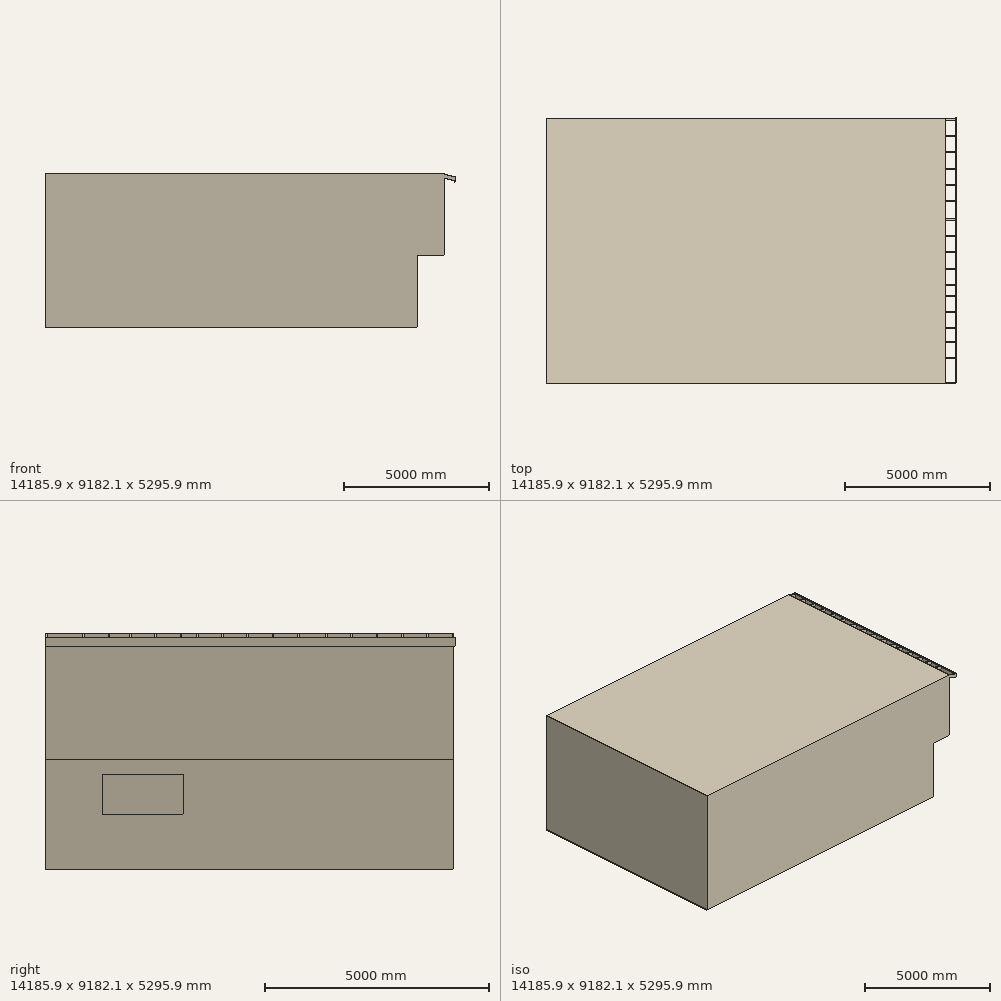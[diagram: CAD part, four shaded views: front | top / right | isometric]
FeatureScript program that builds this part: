
annotation { "Feature Type Name" : "Feature", "Feature Type Description" : "" }
export const myFeature = defineFeature(function(context is Context, id is Id, definition is map)
    precondition{}
    {
        {
            var Q0;
            Q0=qCreatedBy(makeId("Top.planeOp"),FACE);
            var sketch = newSketch(context, id + "F0", { "sketchPlane" : qUnion([Q0])});
            skLineSegment(sketch, "E0.bottom", {"start": v(6438.9, -4572) * mm, "end": v(-6438.9, -4572) * mm});
            skLineSegment(sketch, "E0.top", {"start": v(6438.9, 4572) * mm, "end": v(-6438.9, 4572) * mm});
            skLineSegment(sketch, "E0.left", {"start": v(6438.9, -4572) * mm, "end": v(6438.9, 4572) * mm});
            skLineSegment(sketch, "E0.right", {"start": v(-6438.9, -4572) * mm, "end": v(-6438.9, 4572) * mm});
            skPoint(sketch, "E0.middle", {"position": v(0, 0) * mm});
            skSolve(sketch);
        }
        {
            var Q0;
            Q0=makeQuery(id+"F0.imprint","IMPRINT",FACE,{"disambiguationData":[TD([[makeQuery(id+"F0.imprint","IMPRINT",EDGE,{"derivedFrom":sQuery(id+"F0.wireOp",EDGE,"E0.bottom")}),-1.0]])]});
            extrude(context, id + "F1", {"entities" : qUnion([Q0]), "depth" : 5295.9 * mm});
        }
        {
            var Q0;
            Q0=makeQuery(id+"F1.opExtrude","SWEPT_FACE",FACE,{"disambiguationData":[OSD([sQuery(id+"F0.wireOp",EDGE,"E0.left")])]});
            var sketch = newSketch(context, id + "F2", { "sketchPlane" : qUnion([Q0])});
            skLineSegment(sketch, "E1.bottom", {"start": v(-4572, 2476.5) * mm, "end": v(4572, 2476.5) * mm});
            skLineSegment(sketch, "E1.top", {"start": v(-4572, 5295.9) * mm, "end": v(4572, 5295.9) * mm});
            skLineSegment(sketch, "E1.left", {"start": v(-4572, 2476.5) * mm, "end": v(-4572, 5295.9) * mm});
            skLineSegment(sketch, "E1.right", {"start": v(4572, 2476.5) * mm, "end": v(4572, 5295.9) * mm});
            skSolve(sketch);
        }
        {
            var Q0;
            Q0 = qSketchRegion(id + "F2", true);
            extrude(context, id + "F3", {"entities" : qUnion([Q0]), "operationType" : NewBodyOperationType.ADD, "depth" : 914.4 * mm});
        }
        {
            var Q0;
            Q0=makeQuery(id+"F1.opExtrude","SWEPT_FACE",FACE,{"disambiguationData":[OSD([sQuery(id+"F0.wireOp",EDGE,"E0.left")])]});
            var sketch = newSketch(context, id + "F4", { "sketchPlane" : qUnion([Q0])});
            skLineSegment(sketch, "E2.bottom", {"start": v(-3289.3, 1244.6) * mm, "end": v(-1485.9, 1244.6) * mm});
            skLineSegment(sketch, "E2.top", {"start": v(-3289.3, 2133.6) * mm, "end": v(-1485.9, 2133.6) * mm});
            skLineSegment(sketch, "E2.left", {"start": v(-3289.3, 1244.6) * mm, "end": v(-3289.3, 2133.6) * mm});
            skLineSegment(sketch, "E2.right", {"start": v(-1485.9, 1244.6) * mm, "end": v(-1485.9, 2133.6) * mm});
            skSolve(sketch);
        }
        {
            var Q0;
            Q0 = qSketchRegion(id + "F4", true);
            extrude(context, id + "F5", {"entities" : qUnion([Q0]), "operationType" : NewBodyOperationType.REMOVE, "oppositeDirection" : true, "depth" : 30.48 * mm});
        }
        {
            var Q0;
            Q0=makeQuery(id+"F3.opExtrude","CAP_FACE",FACE,{"disambiguationData":[OSD([sQuery(id+"F2.wireOp",EDGE,"E1.bottom"),sQuery(id+"F2.wireOp",EDGE,"E1.top"),sQuery(id+"F2.wireOp",EDGE,"E1.left"),sQuery(id+"F2.wireOp",EDGE,"E1.right")])],"isStart":false});
            var sketch = newSketch(context, id + "F6", { "sketchPlane" : qUnion([Q0])});
            skLineSegment(sketch, "E3.bottom", {"start": v(-4572, 5295.9) * mm, "end": v(-4533.9, 5295.9) * mm});
            skLineSegment(sketch, "E3.top", {"start": v(-4572, 5156.2) * mm, "end": v(-4533.9, 5156.2) * mm});
            skLineSegment(sketch, "E3.left", {"start": v(-4572, 5295.9) * mm, "end": v(-4572, 5156.2) * mm});
            skLineSegment(sketch, "E3.right", {"start": v(-4533.9, 5295.9) * mm, "end": v(-4533.9, 5156.2) * mm});
            skLineSegment(sketch, "E4.bottom", {"start": v(-3733.8, 5295.9) * mm, "end": v(-3695.7, 5295.9) * mm});
            skLineSegment(sketch, "E4.top", {"start": v(-3733.8, 5156.2) * mm, "end": v(-3695.7, 5156.2) * mm});
            skLineSegment(sketch, "E4.left", {"start": v(-3733.8, 5295.9) * mm, "end": v(-3733.8, 5156.2) * mm});
            skLineSegment(sketch, "E4.right", {"start": v(-3695.7, 5295.9) * mm, "end": v(-3695.7, 5156.2) * mm});
            skLineSegment(sketch, "E5.bottom", {"start": v(-3167.38, 5156.2) * mm, "end": v(-3129.28, 5156.2) * mm});
            skLineSegment(sketch, "E5.top", {"start": v(-3167.38, 5295.9) * mm, "end": v(-3129.28, 5295.9) * mm});
            skLineSegment(sketch, "E5.left", {"start": v(-3167.38, 5156.2) * mm, "end": v(-3167.38, 5295.9) * mm});
            skLineSegment(sketch, "E5.right", {"start": v(-3129.28, 5156.2) * mm, "end": v(-3129.28, 5295.9) * mm});
            skLineSegment(sketch, "E6.bottom", {"start": v(-2692.4, 5156.2) * mm, "end": v(-2654.3, 5156.2) * mm});
            skLineSegment(sketch, "E6.top", {"start": v(-2692.4, 5295.9) * mm, "end": v(-2654.3, 5295.9) * mm});
            skLineSegment(sketch, "E6.left", {"start": v(-2692.4, 5156.2) * mm, "end": v(-2692.4, 5295.9) * mm});
            skLineSegment(sketch, "E6.right", {"start": v(-2654.3, 5156.2) * mm, "end": v(-2654.3, 5295.9) * mm});
            skLineSegment(sketch, "E7.bottom", {"start": v(-2125.98, 5156.2) * mm, "end": v(-2087.88, 5156.2) * mm});
            skLineSegment(sketch, "E7.top", {"start": v(-2125.98, 5295.9) * mm, "end": v(-2087.88, 5295.9) * mm});
            skLineSegment(sketch, "E7.left", {"start": v(-2125.98, 5156.2) * mm, "end": v(-2125.98, 5295.9) * mm});
            skLineSegment(sketch, "E7.right", {"start": v(-2087.88, 5156.2) * mm, "end": v(-2087.88, 5295.9) * mm});
            skLineSegment(sketch, "E8.bottom", {"start": v(-1559.56, 5156.2) * mm, "end": v(-1521.46, 5156.2) * mm});
            skLineSegment(sketch, "E8.top", {"start": v(-1559.56, 5295.9) * mm, "end": v(-1521.46, 5295.9) * mm});
            skLineSegment(sketch, "E8.left", {"start": v(-1559.56, 5156.2) * mm, "end": v(-1559.56, 5295.9) * mm});
            skLineSegment(sketch, "E8.right", {"start": v(-1521.46, 5156.2) * mm, "end": v(-1521.46, 5295.9) * mm});
            skLineSegment(sketch, "E9.bottom", {"start": v(-1193.8, 5156.2) * mm, "end": v(-1155.7, 5156.2) * mm});
            skLineSegment(sketch, "E9.top", {"start": v(-1193.8, 5295.9) * mm, "end": v(-1155.7, 5295.9) * mm});
            skLineSegment(sketch, "E9.left", {"start": v(-1193.8, 5156.2) * mm, "end": v(-1193.8, 5295.9) * mm});
            skLineSegment(sketch, "E9.right", {"start": v(-1155.7, 5156.2) * mm, "end": v(-1155.7, 5295.9) * mm});
            skLineSegment(sketch, "E10.bottom", {"start": v(-627.38, 5156.2) * mm, "end": v(-589.28, 5156.2) * mm});
            skLineSegment(sketch, "E10.top", {"start": v(-627.38, 5295.9) * mm, "end": v(-589.28, 5295.9) * mm});
            skLineSegment(sketch, "E10.left", {"start": v(-627.38, 5156.2) * mm, "end": v(-627.38, 5295.9) * mm});
            skLineSegment(sketch, "E10.right", {"start": v(-589.28, 5156.2) * mm, "end": v(-589.28, 5295.9) * mm});
            skLineSegment(sketch, "E11.bottom", {"start": v(-60.96, 5156.2) * mm, "end": v(-22.86, 5156.2) * mm});
            skLineSegment(sketch, "E11.top", {"start": v(-60.96, 5295.9) * mm, "end": v(-22.86, 5295.9) * mm});
            skLineSegment(sketch, "E11.left", {"start": v(-60.96, 5156.2) * mm, "end": v(-60.96, 5295.9) * mm});
            skLineSegment(sketch, "E11.right", {"start": v(-22.86, 5156.2) * mm, "end": v(-22.86, 5295.9) * mm});
            skLineSegment(sketch, "E12.bottom", {"start": v(505.46, 5156.2) * mm, "end": v(543.56, 5156.2) * mm});
            skLineSegment(sketch, "E12.top", {"start": v(505.46, 5295.9) * mm, "end": v(543.56, 5295.9) * mm});
            skLineSegment(sketch, "E12.left", {"start": v(505.46, 5156.2) * mm, "end": v(505.46, 5295.9) * mm});
            skLineSegment(sketch, "E12.right", {"start": v(543.56, 5156.2) * mm, "end": v(543.56, 5295.9) * mm});
            skLineSegment(sketch, "E13.bottom", {"start": v(1071.88, 5156.2) * mm, "end": v(1109.98, 5156.2) * mm});
            skLineSegment(sketch, "E13.top", {"start": v(1071.88, 5295.9) * mm, "end": v(1109.98, 5295.9) * mm});
            skLineSegment(sketch, "E13.left", {"start": v(1071.88, 5156.2) * mm, "end": v(1071.88, 5295.9) * mm});
            skLineSegment(sketch, "E13.right", {"start": v(1109.98, 5156.2) * mm, "end": v(1109.98, 5295.9) * mm});
            skLineSegment(sketch, "E14.bottom", {"start": v(1701.8, 5156.2) * mm, "end": v(1739.9, 5156.2) * mm});
            skLineSegment(sketch, "E14.top", {"start": v(1701.8, 5295.9) * mm, "end": v(1739.9, 5295.9) * mm});
            skLineSegment(sketch, "E14.left", {"start": v(1701.8, 5156.2) * mm, "end": v(1701.8, 5295.9) * mm});
            skLineSegment(sketch, "E14.right", {"start": v(1739.9, 5156.2) * mm, "end": v(1739.9, 5295.9) * mm});
            skLineSegment(sketch, "E15.bottom", {"start": v(2268.22, 5156.2) * mm, "end": v(2306.32, 5156.2) * mm});
            skLineSegment(sketch, "E15.top", {"start": v(2268.22, 5295.9) * mm, "end": v(2306.32, 5295.9) * mm});
            skLineSegment(sketch, "E15.left", {"start": v(2268.22, 5156.2) * mm, "end": v(2268.22, 5295.9) * mm});
            skLineSegment(sketch, "E15.right", {"start": v(2306.32, 5156.2) * mm, "end": v(2306.32, 5295.9) * mm});
            skLineSegment(sketch, "E16.bottom", {"start": v(2834.64, 5156.2) * mm, "end": v(2872.74, 5156.2) * mm});
            skLineSegment(sketch, "E16.top", {"start": v(2834.64, 5295.9) * mm, "end": v(2872.74, 5295.9) * mm});
            skLineSegment(sketch, "E16.left", {"start": v(2834.64, 5156.2) * mm, "end": v(2834.64, 5295.9) * mm});
            skLineSegment(sketch, "E16.right", {"start": v(2872.74, 5156.2) * mm, "end": v(2872.74, 5295.9) * mm});
            skLineSegment(sketch, "E17.bottom", {"start": v(3401.06, 5156.2) * mm, "end": v(3439.16, 5156.2) * mm});
            skLineSegment(sketch, "E17.top", {"start": v(3401.06, 5295.9) * mm, "end": v(3439.16, 5295.9) * mm});
            skLineSegment(sketch, "E17.left", {"start": v(3401.06, 5156.2) * mm, "end": v(3401.06, 5295.9) * mm});
            skLineSegment(sketch, "E17.right", {"start": v(3439.16, 5156.2) * mm, "end": v(3439.16, 5295.9) * mm});
            skLineSegment(sketch, "E18.bottom", {"start": v(3967.48, 5156.2) * mm, "end": v(4005.58, 5156.2) * mm});
            skLineSegment(sketch, "E18.top", {"start": v(3967.48, 5295.9) * mm, "end": v(4005.58, 5295.9) * mm});
            skLineSegment(sketch, "E18.left", {"start": v(3967.48, 5156.2) * mm, "end": v(3967.48, 5295.9) * mm});
            skLineSegment(sketch, "E18.right", {"start": v(4005.58, 5156.2) * mm, "end": v(4005.58, 5295.9) * mm});
            skLineSegment(sketch, "E19.bottom", {"start": v(4533.9, 5156.2) * mm, "end": v(4572, 5156.2) * mm});
            skLineSegment(sketch, "E19.top", {"start": v(4533.9, 5295.9) * mm, "end": v(4572, 5295.9) * mm});
            skLineSegment(sketch, "E19.left", {"start": v(4533.9, 5156.2) * mm, "end": v(4533.9, 5295.9) * mm});
            skLineSegment(sketch, "E19.right", {"start": v(4572, 5156.2) * mm, "end": v(4572, 5295.9) * mm});
            skLineSegment(sketch, "E20", {"start": v(-3695.7, 5156.2) * mm, "end": v(-3167.38, 5156.2) * mm, "construction": true});
            skLineSegment(sketch, "E21", {"start": v(-2654.3, 5156.2) * mm, "end": v(-2125.98, 5156.2) * mm, "construction": true});
            skLineSegment(sketch, "E22", {"start": v(-2087.88, 5156.2) * mm, "end": v(-1559.56, 5156.2) * mm, "construction": true});
            skLineSegment(sketch, "E23", {"start": v(-1155.7, 5156.2) * mm, "end": v(-627.38, 5156.2) * mm, "construction": true});
            skLineSegment(sketch, "E24", {"start": v(-589.28, 5156.2) * mm, "end": v(-60.96, 5156.2) * mm, "construction": true});
            skLineSegment(sketch, "E25", {"start": v(-22.86, 5156.2) * mm, "end": v(505.46, 5156.2) * mm, "construction": true});
            skLineSegment(sketch, "E26", {"start": v(543.56, 5156.2) * mm, "end": v(1071.88, 5156.2) * mm, "construction": true});
            skLineSegment(sketch, "E27", {"start": v(1739.9, 5156.2) * mm, "end": v(2268.22, 5156.2) * mm, "construction": true});
            skLineSegment(sketch, "E28", {"start": v(2306.32, 5156.2) * mm, "end": v(2834.64, 5156.2) * mm, "construction": true});
            skLineSegment(sketch, "E29", {"start": v(2872.74, 5156.2) * mm, "end": v(3401.06, 5156.2) * mm, "construction": true});
            skLineSegment(sketch, "E30", {"start": v(3439.16, 5156.2) * mm, "end": v(3967.48, 5156.2) * mm, "construction": true});
            skLineSegment(sketch, "E31", {"start": v(4005.58, 5156.2) * mm, "end": v(4533.9, 5156.2) * mm, "construction": true});
            skSolve(sketch);
        }
        {
            var Q0;
            Q0=makeQuery(id+"F3.boolean.opBoolean","MERGE",FACE,{"derivedFrom":[makeQuery(id+"F1.opExtrude","SWEPT_FACE",FACE,{"disambiguationData":[OSD([sQuery(id+"F0.wireOp",EDGE,"E0.bottom")])]}),makeQuery(id+"F3.opExtrude","SWEPT_FACE",FACE,{"disambiguationData":[OSD([sQuery(id+"F2.wireOp",EDGE,"E1.left")])]})]});
            var sketch = newSketch(context, id + "F7", { "sketchPlane" : qUnion([Q0])});
            skLineSegment(sketch, "E32", {"start": v(7708.9, 5196.55) * mm, "end": v(7353.3, 2476.5) * mm, "construction": true});
            skLineSegment(sketch, "E33", {"start": v(7353.3, 5295.9) * mm, "end": v(7708.9, 5295.9) * mm, "construction": true});
            skLineSegment(sketch, "E34", {"start": v(7353.3, 5295.9) * mm, "end": v(7708.9, 5196.55) * mm});
            skSolve(sketch);
        }
        {
            var Q0;
            Q0 = qSketchRegion(id + "F6", true);
            var Q1;
            Q1=sQuery(id+"F7.wireOp",EDGE,"E34");
            sweep(context, id + "F8", {"operationType" : NewBodyOperationType.ADD, "profiles" : qUnion([Q0]), "path" : qUnion([Q1])});
        }
        {
            var Q0;
            Q0=makeQuery(id+"F8.opSweep","CAP_FACE",FACE,{"disambiguationData":[OSD([sQuery(id+"F6.wireOp",EDGE,"E3.bottom"),sQuery(id+"F6.wireOp",EDGE,"E3.top"),sQuery(id+"F6.wireOp",EDGE,"E3.left"),sQuery(id+"F6.wireOp",EDGE,"E3.right"),sQuery(id+"F7.wireOp",VERTEX,"E34.end")])],"isStart":false});
            extrude(context, id + "F9", {"entities" : qUnion([Q0]), "operationType" : NewBodyOperationType.ADD, "depth" : 38.1 * mm});
        }
        {
            var Q0;
            Q0=makeQuery(id+"F9.opExtrude","SWEPT_FACE",FACE,{"disambiguationData":[OSD([sQuery(id+"F6.wireOp",EDGE,"E3.top"),sQuery(id+"F7.wireOp",VERTEX,"E34.end")])]});
            extrude(context, id + "F10", {"entities" : qUnion([Q0]), "operationType" : NewBodyOperationType.ADD, "depth" : 50.8 * mm});
        }
        {
            var Q0;
            {var subQ0=sQuery(id+"F7.wireOp",EDGE,"E34");var subQ1=sQuery(id+"F6.wireOp",EDGE,"E3.right");Q0=makeQuery(id+"F10.boolean.opBoolean","MERGE",FACE,{"derivedFrom":[makeQuery(id+"F9.boolean.opBoolean","MERGE",FACE,{"derivedFrom":[makeQuery(id+"F8.opSweep","SWEPT_FACE",FACE,{"disambiguationData":[OSD([subQ1,subQ0])]}),makeQuery(id+"F9.opExtrude","SWEPT_FACE",FACE,{"disambiguationData":[OSD([subQ1,sQuery(id+"F7.wireOp",VERTEX,"E34.end")])]})]}),makeQuery(id+"F10.opExtrude","SWEPT_FACE",FACE,{"disambiguationData":[OSD([sQuery(id+"F6.wireOp",EDGE,"E3.top"),subQ1,subQ0])]})]});}
            var sketch = newSketch(context, id + "F11", { "sketchPlane" : qUnion([Q0])});
            skLineSegment(sketch, "E35.bottom", {"start": v(-7747, 5196.55) * mm, "end": v(-7708.9, 5196.55) * mm});
            skLineSegment(sketch, "E35.top", {"start": v(-7747, 5006.05) * mm, "end": v(-7708.9, 5006.05) * mm});
            skLineSegment(sketch, "E35.left", {"start": v(-7747, 5196.55) * mm, "end": v(-7747, 5006.05) * mm});
            skLineSegment(sketch, "E35.right", {"start": v(-7708.9, 5196.55) * mm, "end": v(-7708.9, 5006.05) * mm});
            skSolve(sketch);
        }
        {
            var Q0;
            {var subQ1=sQuery(id+"F11.wireOp",EDGE,"E35.bottom");Q0=makeQuery(id+"F11.imprint","IMPRINT",FACE,{"disambiguationData":[TD([[makeQuery(id+"F11.imprint","IMPRINT",EDGE,{"derivedFrom":subQ1}),-1.0]])]});}
            extrude(context, id + "F12", {"entities" : qUnion([Q0]), "operationType" : NewBodyOperationType.ADD, "depth" : 9144 * mm});
        }
    });
